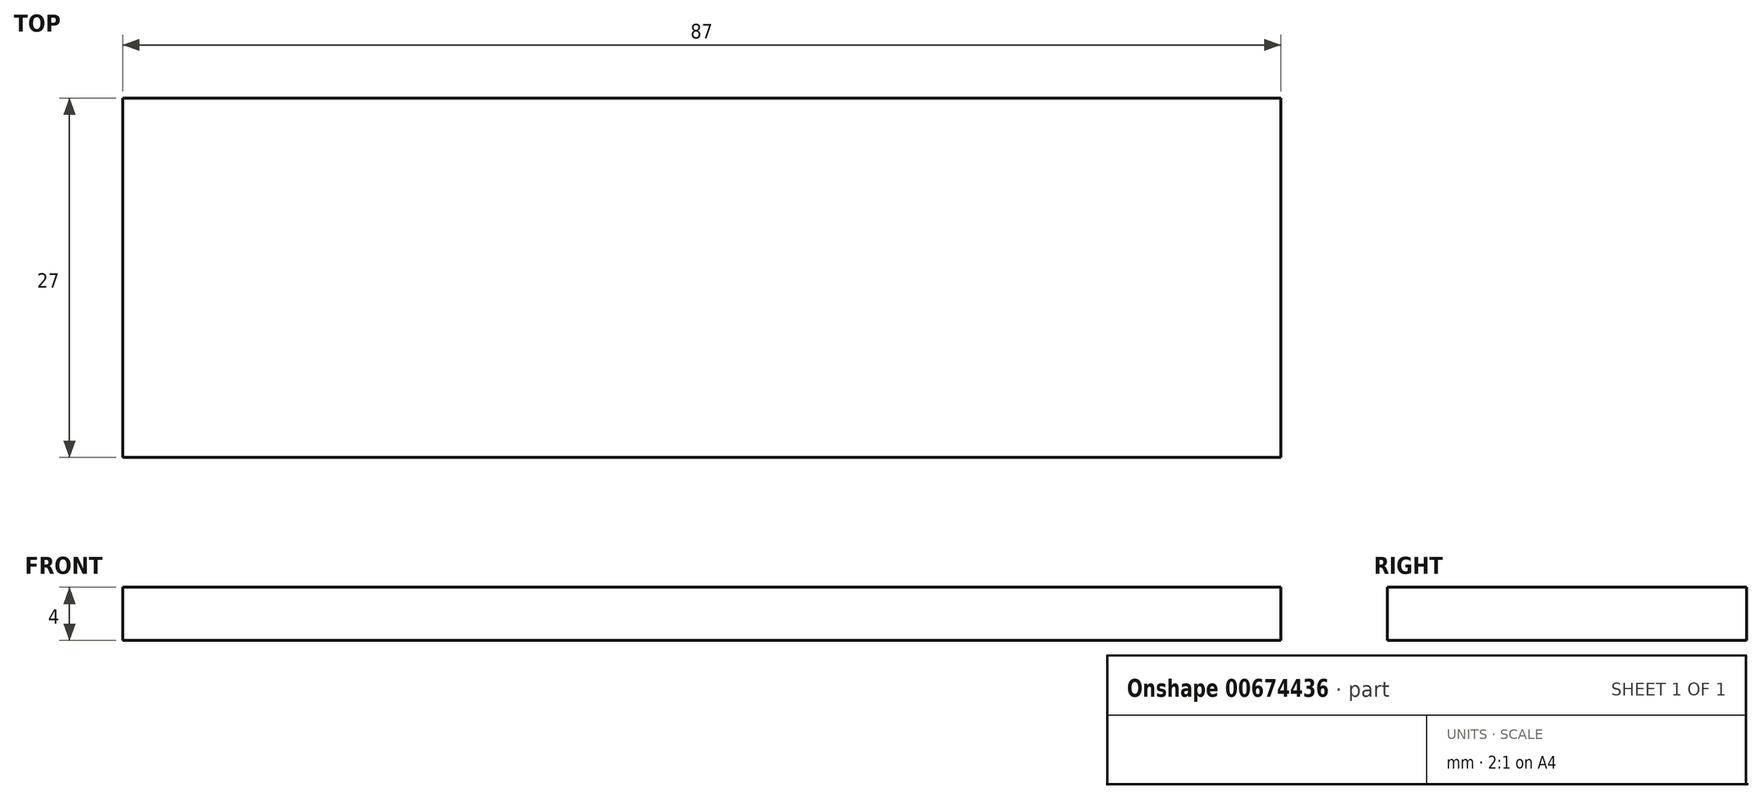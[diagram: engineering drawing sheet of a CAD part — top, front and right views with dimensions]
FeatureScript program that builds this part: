
annotation { "Feature Type Name" : "Feature", "Feature Type Description" : "" }
export const myFeature = defineFeature(function(context is Context, id is Id, definition is map)
    precondition{}
    {
        {
            var Q0;
            Q0=qCreatedBy(makeId("Top.planeOp"),FACE);
            var sketch = newSketch(context, id + "F0", { "sketchPlane" : qUnion([Q0])});
            skLineSegment(sketch, "E0.bottom", {"start": v(0, 0) * mm, "end": v(-87, 0) * mm});
            skLineSegment(sketch, "E0.top", {"start": v(0, 27) * mm, "end": v(-87, 27) * mm});
            skLineSegment(sketch, "E0.left", {"start": v(0, 0) * mm, "end": v(0, 27) * mm});
            skLineSegment(sketch, "E0.right", {"start": v(-87, 0) * mm, "end": v(-87, 27) * mm});
            skSolve(sketch);
        }
        {
            var Q0;
            Q0=makeQuery(id+"F0.imprint","IMPRINT",FACE,{"disambiguationData":[TD([[makeQuery(id+"F0.imprint","IMPRINT",EDGE,{"derivedFrom":sQuery(id+"F0.wireOp",EDGE,"E0.bottom")}),-1.0]])]});
            extrude(context, id + "F1", {"entities" : qUnion([Q0]), "depth" : 4 * mm, "offsetDistance" : 25.4 * mm});
        }
    });
